# Revit family: 94750-221
name_source: partatom
category: Modelos genéricos
revit_build: Autodesk Revit 2016 (Build: 20150220_1215(x64)
units: mm (PartAtom-declared; Revit-internal decimal feet)

## family parameters
Compartilhado = Não
Corte com vazios quando carregados = Não
Cota do conector redondo = Utilizar diâmetro
Hospedeiro = Face
Pode hospedar o vergalhão = Não
Ponto de cálculo do ambiente = Não
Tipo de parte = Normal

## types (1)
- Dominó Slider 2EI 30
    Código de montagem = Domino Slider 2EI 30 - Ref. 9475022
    Descrição = Domino Slider 2EI 30 - Ref. 9475022
    Elevação-padrão = 1219.2  [stored 4 ft]
    Fabricante = Tramontina
    Frequencia = 60 Hz
    Modelo = Domino Slider 2EI 30 - Ref. 94750221
    Nicho de Instalação = 265 x 495
    Potencia Eletrica Total = 3500 W
    Potencia Eletrica das Areas de Aquecimento - 160 diametro = 1,5 Kw
    Potencia Eletrica das Areas de Aquecimento - 180 diametro = 1,7 kW
    Tensão = 220 V
    URL = tramontina.com.br

note: [stored X ft] marks values corroborated as IEEE doubles in the binary element streams (Revit-internal decimal feet)
